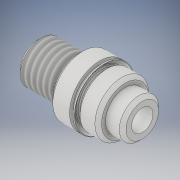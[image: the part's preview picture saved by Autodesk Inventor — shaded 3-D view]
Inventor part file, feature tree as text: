
AUTODESK INVENTOR PART (.ipt)
format: ipt  version: 2018 (Build 220112000, 112)  size: 240,640 bytes
history: native  units: in
note: dims shown in document units (in); Inventor stores cm internally (conversion verified against a paired STEP export)
features: other x84, sketch x5, revolve x4, thread x1, hole x1
ambient origin geometry x8: Origin, YZ Plane, XZ Plane, XY Plane, X Axis, Y Axis, Z Axis, Center Point
bodies: Solid1 (feature_tree)
feature tree (95):
  revolve  "Revolution1"  [1 undecoded]
  thread  "Thread1"  [1 undecoded]
  revolve  "Revolution2"  Angle=360.0deg
  revolve  "Revolution3"  [1 undecoded]
  hole  "Hole1"  [1 undecoded]
  revolve  "Revolution4"  [1 undecoded]
  other  "hh_XY"
  other  "hh_YZ"
  other  "hh_ZX"
  other  "hh_X"
  other  "hh_Y"
  other  "hh_Z"
  other  "hh_Center"
  other  "rod_guide_XY"
  other  "rod_guide_YZ"
  other  "rod_guide_ZX"
  other  "rod_guide_X"
  other  "rod_guide_Y"
  other  "rod_guide_Z"
  other  "rod_guide_Center"
  other  "t1_XY"
  other  "t1_YZ"
  other  "t1_ZX"
  other  "t1_X"
  other  "t1_Y"
  other  "t1_Z"
  other  "t1_Center"
  other  "t111_XY"
  other  "t111_YZ"
  other  "t111_ZX"
  other  "t111_X"
  other  "t111_Y"
  other  "t111_Z"
  other  "t111_Center"
  other  "to_foot_bracket_XY"
  other  "to_foot_bracket_YZ"
  other  "to_foot_bracket_ZX"
  other  "to_foot_bracket_X"
  other  "to_foot_bracket_Y"
  other  "to_foot_bracket_Z"
  other  "to_foot_bracket_Center"
  other  "to_nut_XY"
  other  "to_nut_YZ"
  other  "to_nut_ZX"
  other  "to_nut_X"
  other  "to_nut_Y"
  other  "to_nut_Z"
  other  "to_nut_Center"
  other  "to_rod_XY"
  other  "to_rod_YZ"
  other  "to_rod_ZX"
  other  "to_rod_X"
  other  "to_rod_Y"
  other  "to_rod_Z"
  other  "to_rod_Center"
  other  "to_screw_XY"
  other  "to_screw_YZ"
  other  "to_screw_ZX"
  other  "to_screw_X"
  other  "to_screw_Y"
  other  "to_screw_Z"
  other  "to_screw_Center"
  other  "to_trunnion_brackets_XY"
  other  "to_trunnion_brackets_YZ"
  other  "to_trunnion_brackets_ZX"
  other  "to_trunnion_brackets_X"
  other  "to_trunnion_brackets_Y"
  other  "to_trunnion_brackets_Z"
  other  "to_trunnion_brackets_Center"
  other  "to_trunnion_brackets1_XY"
  other  "to_trunnion_brackets1_YZ"
  other  "to_trunnion_brackets1_ZX"
  other  "to_trunnion_brackets1_X"
  other  "to_trunnion_brackets1_Y"
  other  "to_trunnion_brackets1_Z"
  other  "to_trunnion_brackets1_Center"
  other  "to_trunnion_brackets2_XY"
  other  "to_trunnion_brackets2_YZ"
  other  "to_trunnion_brackets2_ZX"
  other  "to_trunnion_brackets2_X"
  other  "to_trunnion_brackets2_Y"
  other  "to_trunnion_brackets2_Z"
  other  "to_trunnion_brackets2_Center"
  other  "to_tube_XY"
  other  "to_tube_YZ"
  other  "to_tube_ZX"
  other  "to_tube_X"
  other  "to_tube_Y"
  other  "to_tube_Z"
  other  "to_tube_Center"
  sketch  "Sketch_1"  dims[d0=360.0deg d1=0.2287in d2=0.0in d3=360.0deg]
  sketch  "Sketch_3"  dims[d4=360.0deg]
  sketch  "Sketch_4"  dims[d5=0.128in d6=0.75in d7=0.158in d8=0.25in d9=90.0deg d10=0.625in d11=0.0in d12=360.0deg]
  sketch  "Sketch4"  dims[d13=0.0in d14=0.0in d15=0.0in d16=0.0in d17=0.0in d18=0.0in]
  sketch  "Sketch_47"
note: 5 required parameter values undecoded (feature->parameter linkage not recoverable at this tier; creation-order binding heuristic only, values carry confidence <= 0.55)